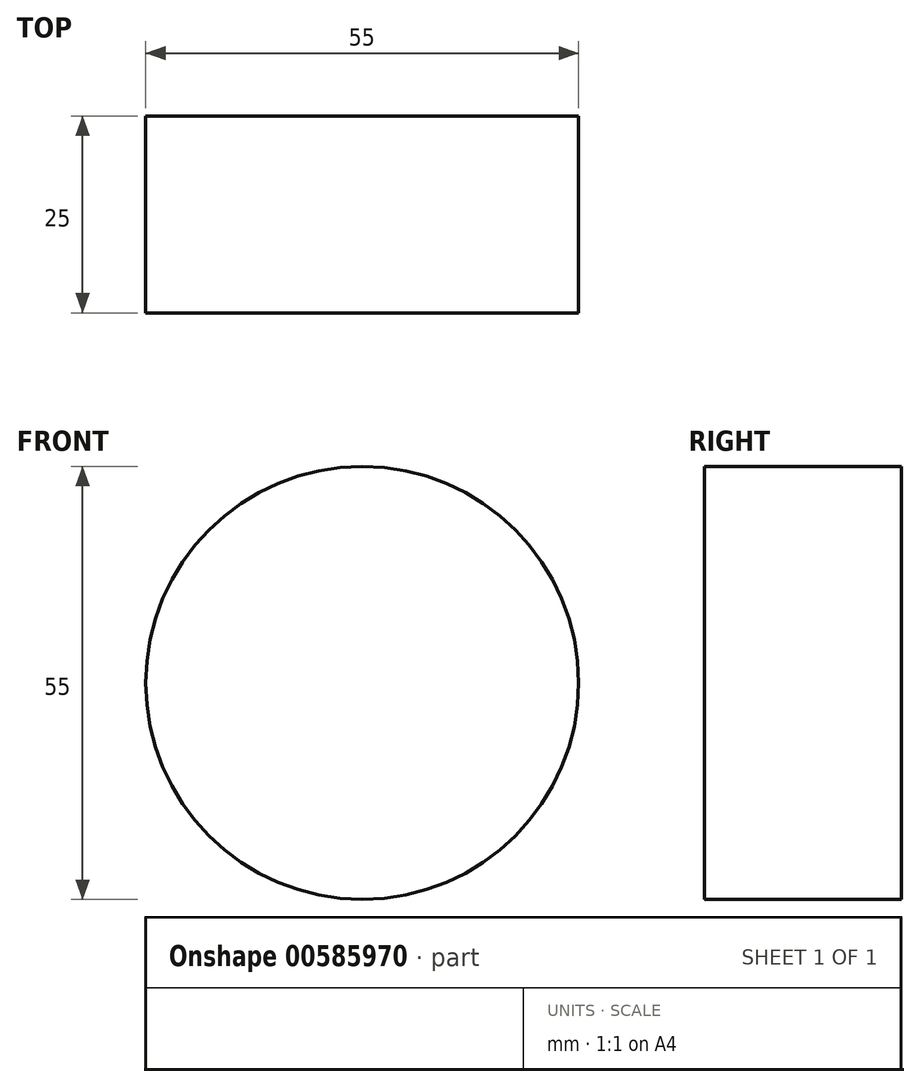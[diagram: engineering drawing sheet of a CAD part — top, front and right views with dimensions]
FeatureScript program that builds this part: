
annotation { "Feature Type Name" : "Feature", "Feature Type Description" : "" }
export const myFeature = defineFeature(function(context is Context, id is Id, definition is map)
    precondition{}
    {
        {
            var Q0;
            Q0=qCreatedBy(makeId("Front.planeOp"),FACE);
            var sketch = newSketch(context, id + "F0", { "sketchPlane" : qUnion([Q0])});
            skCircle(sketch, "E0", {"center": v(-45.97, 31.44) * mm, "radius": 27.5 * mm});
            skSolve(sketch);
        }
        {
            var Q0;
            Q0=makeQuery(id+"F0.imprint","IMPRINT",FACE,{"disambiguationData":[TD([[makeQuery(id+"F0.imprint","IMPRINT",EDGE,{"derivedFrom":sQuery(id+"F0.wireOp",EDGE,"E0")}),1.0]])]});
            extrude(context, id + "F1", {"entities" : qUnion([Q0]), "oppositeDirection" : true, "depth" : 25 * mm, "offsetDistance" : 25 * mm});
        }
    });
